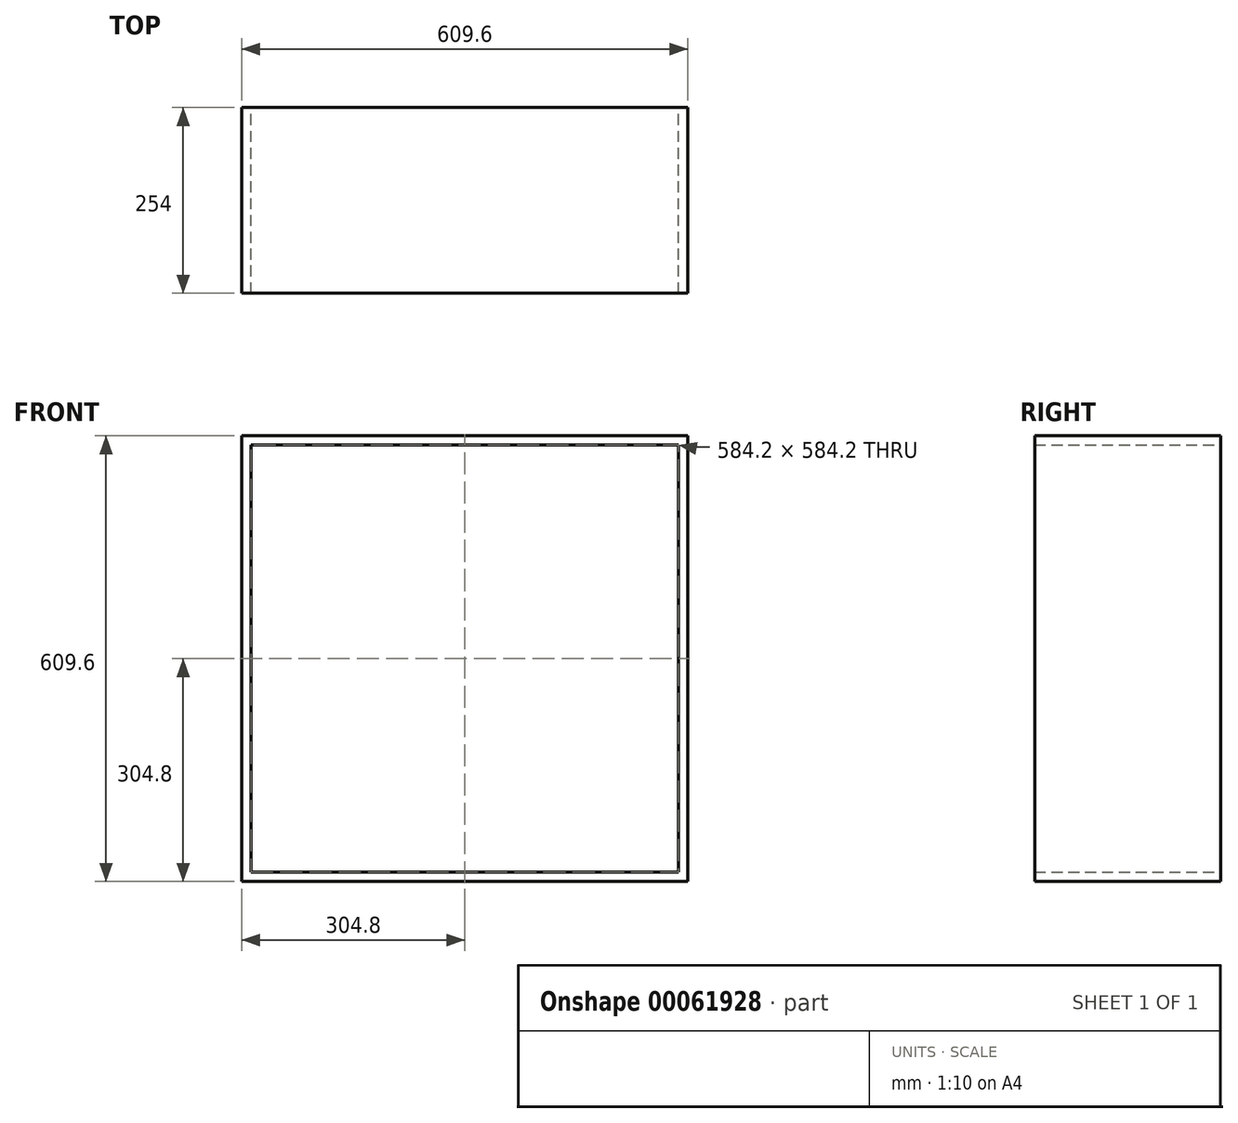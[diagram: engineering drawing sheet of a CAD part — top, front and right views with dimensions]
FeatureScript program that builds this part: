
annotation { "Feature Type Name" : "Feature", "Feature Type Description" : "" }
export const myFeature = defineFeature(function(context is Context, id is Id, definition is map)
    precondition{}
    {
        {
            var Q0;
            Q0=qCreatedBy(makeId("Front.planeOp"),FACE);
            var sketch = newSketch(context, id + "F0", { "sketchPlane" : qUnion([Q0])});
            skLineSegment(sketch, "E0.bottom", {"start": v(0, 0) * mm, "end": v(609.6, 0) * mm});
            skLineSegment(sketch, "E0.top", {"start": v(0, 609.6) * mm, "end": v(609.6, 609.6) * mm});
            skLineSegment(sketch, "E0.left", {"start": v(0, 0) * mm, "end": v(0, 609.6) * mm});
            skLineSegment(sketch, "E0.right", {"start": v(609.6, 0) * mm, "end": v(609.6, 609.6) * mm});
            skSolve(sketch);
        }
        {
            var Q0;
            Q0 = qSketchRegion(id + "F0", true);
            extrude(context, id + "F1", {"entities" : qUnion([Q0]), "depth" : 254 * mm});
        }
        {
            var Q0;
            Q0=makeQuery(id+"F1.opExtrude","CAP_FACE",FACE,{"disambiguationData":[OSD([sQuery(id+"F0.wireOp",EDGE,"E0.bottom"),sQuery(id+"F0.wireOp",EDGE,"E0.top"),sQuery(id+"F0.wireOp",EDGE,"E0.left"),sQuery(id+"F0.wireOp",EDGE,"E0.right")])],"isStart":false});
            var Q1;
            Q1=makeQuery(id+"F1.opExtrude","CAP_FACE",FACE,{"disambiguationData":[OSD([sQuery(id+"F0.wireOp",EDGE,"E0.bottom"),sQuery(id+"F0.wireOp",EDGE,"E0.top"),sQuery(id+"F0.wireOp",EDGE,"E0.left"),sQuery(id+"F0.wireOp",EDGE,"E0.right")])],"isStart":true});
            shell(context, id + "F2", {"entities" : qUnion([Q0, Q1]), "thickness" : 12.7 * mm});
        }
    });
